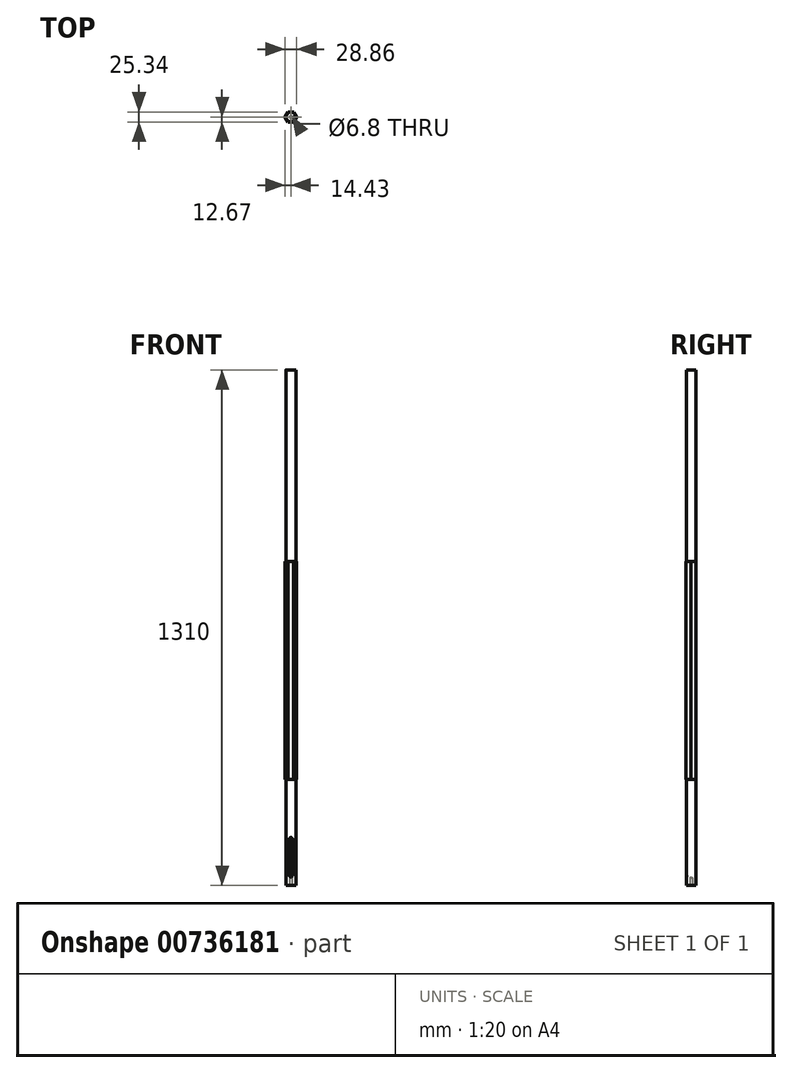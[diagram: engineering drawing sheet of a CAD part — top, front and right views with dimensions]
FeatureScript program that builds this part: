
annotation { "Feature Type Name" : "Feature", "Feature Type Description" : "" }
export const myFeature = defineFeature(function(context is Context, id is Id, definition is map)
    precondition{}
    {
        {
            var Q0;
            Q0=qCreatedBy(makeId("Top.planeOp"),FACE);
            var sketch = newSketch(context, id + "F0", { "sketchPlane" : qUnion([Q0])});
            skCircle(sketch, "E0", {"center": v(0, 0) * mm, "radius": 12.5 * mm});
            skSolve(sketch);
        }
        {
            var Q0;
            Q0=makeQuery(id+"F0.imprint","IMPRINT",FACE,{"disambiguationData":[TD([[makeQuery(id+"F0.imprint","IMPRINT",EDGE,{"derivedFrom":sQuery(id+"F0.wireOp",EDGE,"E0")}),1.0]])]});
            extrude(context, id + "F1", {"entities" : qUnion([Q0]), "depth" : 462 * mm, "offsetDistance" : 25 * mm});
        }
        {
            var Q0;
            Q0=makeQuery(id+"F1.opExtrude","CAP_FACE",FACE,{"disambiguationData":[OSD([sQuery(id+"F0.wireOp",EDGE,"E0")])],"isStart":false});
            var sketch = newSketch(context, id + "F2", { "sketchPlane" : qUnion([Q0])});
            skCircle(sketch, "E1.0", {"center": v(0, 0) * mm, "radius": 12.5 * mm});
            skSolve(sketch);
        }
        {
            var Q0;
            Q0 = qSketchRegion(id + "F2", true);
            extrude(context, id + "F3", {"entities" : qUnion([Q0]), "operationType" : NewBodyOperationType.ADD, "depth" : 25 * mm, "offsetDistance" : 25 * mm});
        }
        {
            var Q0;
            Q0=makeQuery(id+"F1.opExtrude","CAP_FACE",FACE,{"disambiguationData":[OSD([sQuery(id+"F0.wireOp",EDGE,"E0")])],"isStart":true});
            var sketch = newSketch(context, id + "F4", { "sketchPlane" : qUnion([Q0])});
            skCircle(sketch, "E2.cCircle", {"center": v(0, 0) * mm, "radius": 12.5 * mm, "construction": true});
            skLineSegment(sketch, "E2.0", {"start": v(6.92, 12.67) * mm, "end": v(14.43, 0.34) * mm});
            skLineSegment(sketch, "E2.1", {"start": v(14.43, 0.34) * mm, "end": v(7.5, -12.33) * mm});
            skLineSegment(sketch, "E2.2", {"start": v(7.5, -12.33) * mm, "end": v(-6.92, -12.67) * mm});
            skLineSegment(sketch, "E2.3", {"start": v(-6.92, -12.67) * mm, "end": v(-14.43, -0.34) * mm});
            skLineSegment(sketch, "E2.4", {"start": v(-14.43, -0.34) * mm, "end": v(-7.5, 12.33) * mm});
            skLineSegment(sketch, "E2.5", {"start": v(-7.5, 12.33) * mm, "end": v(6.92, 12.67) * mm});
            skPoint(sketch, "E2.0.midPoint", {"position": v(10.68, 6.5) * mm});
            skSolve(sketch);
        }
        {
            var Q0;
            Q0 = qSketchRegion(id + "F4", true);
            extrude(context, id + "F5", {"entities" : qUnion([Q0]), "operationType" : NewBodyOperationType.ADD, "depth" : 553 * mm, "offsetDistance" : 25 * mm});
        }
        {
            var Q0;
            Q0=makeQuery(id+"F5.opExtrude","CAP_FACE",FACE,{"disambiguationData":[OSD([sQuery(id+"F4.wireOp",EDGE,"E2.0"),sQuery(id+"F4.wireOp",EDGE,"E2.1"),sQuery(id+"F4.wireOp",EDGE,"E2.2"),sQuery(id+"F4.wireOp",EDGE,"E2.3"),sQuery(id+"F4.wireOp",EDGE,"E2.4"),sQuery(id+"F4.wireOp",EDGE,"E2.5")])],"isStart":false});
            var sketch = newSketch(context, id + "F6", { "sketchPlane" : qUnion([Q0])});
            skCircle(sketch, "E3", {"center": v(0, 0) * mm, "radius": 12.5 * mm});
            skSolve(sketch);
        }
        {
            var Q0;
            Q0 = qSketchRegion(id + "F6", true);
            extrude(context, id + "F7", {"entities" : qUnion([Q0]), "operationType" : NewBodyOperationType.ADD, "depth" : 270 * mm, "offsetDistance" : 25 * mm});
        }
        {
            var Q0;
            Q0=qCreatedBy(makeId("Front.planeOp"),FACE);
            cPlane(context, id + "F8", {"entities" : qUnion([Q0]), "cplaneType" : CPlaneType.OFFSET, "offset" : 12.5 * mm, "width" : 150 * mm, "height" : 150 * mm});
        }
        {
            var Q0;
            Q0=qCreatedBy(id+"F8.planeOp",FACE);
            var sketch = newSketch(context, id + "F9", { "sketchPlane" : qUnion([Q0])});
            skLineSegment(sketch, "E4.left", {"start": v(3.81, -797.19) * mm, "end": v(3.81, -704.81) * mm});
            skLineSegment(sketch, "E4.right", {"start": v(-3.8, -797.19) * mm, "end": v(-3.8, -704.81) * mm});
            skPoint(sketch, "E4.middle", {"position": v(0, -751) * mm});
            skArc(sketch, "E5", {"start": v(3.81, -704.81) * mm, "mid": v(0, -701) * mm, "end": v(-3.81, -704.81) * mm});
            skPoint(sketch, "E5.centerSnap0", {"position": v(0, -701) * mm});
            skArc(sketch, "E6", {"start": v(-3.81, -797.19) * mm, "mid": v(0, -801) * mm, "end": v(3.81, -797.19) * mm});
            skPoint(sketch, "E7.orphan", {"position": v(-3.81, -801) * mm});
            skPoint(sketch, "E8.orphan", {"position": v(3.81, -801) * mm});
            skPoint(sketch, "E9.orphan", {"position": v(-3.8, -701) * mm});
            skPoint(sketch, "E10.orphan", {"position": v(3.81, -701) * mm});
            skPoint(sketch, "E11", {"position": v(0, -801) * mm});
            skSolve(sketch);
        }
        {
            var Q0;
            Q0 = qSketchRegion(id + "F9", true);
            extrude(context, id + "F10", {"entities" : qUnion([Q0]), "operationType" : NewBodyOperationType.REMOVE, "oppositeDirection" : true, "depth" : 2.5 * mm, "offsetDistance" : 25 * mm});
        }
        {
            var Q0;
            Q0=makeQuery(id+"F7.opExtrude","CAP_FACE",FACE,{"disambiguationData":[OSD([sQuery(id+"F6.wireOp",EDGE,"E3")])],"isStart":false});
            var sketch = newSketch(context, id + "F11", { "sketchPlane" : qUnion([Q0])});
            skPoint(sketch, "E12", {"position": v(0, 0) * mm});
            skSolve(sketch);
        }
        {
            var Q0;
            Q0=sQuery(id+"F11.wireOp",VERTEX,"E12");
            var Q1;
            Q1=makeQuery(id+"F1.opExtrude","SWEPT_BODY",BODY,{"disambiguationData":[OSD([sQuery(id+"F0.wireOp",EDGE,"E0")])]});
            hole(context, id + "F12", {"style" : HoleStyle.SIMPLE, "endStyle" : HoleEndStyle.BLIND, "standardTappedOrClearance" : lookupTablePath({ "standard" : "ISO", "engagement" : "75%", "pitch" : "1.25 mm", "size" : "M8", "type" : "Tapped" }), "standardBlindInLast" : lookupTablePath({ "standard" : "ISO", "engagement" : "75%", "pitch" : "1.25 mm", "size" : "M8", "type" : "Tapped" }), "holeDiameter" : 6.8 * mm, "majorDiameter" : 8 * mm, "showTappedDepth" : true, "holeDepth" : 20 * mm, "isTappedThrough" : true, "tappedDepth" : 16.25 * mm, "tapClearance" : 3, "startFromSketch" : true, "locations" : qUnion([Q0]), "scope" : qUnion([Q1])});
        }
    });
